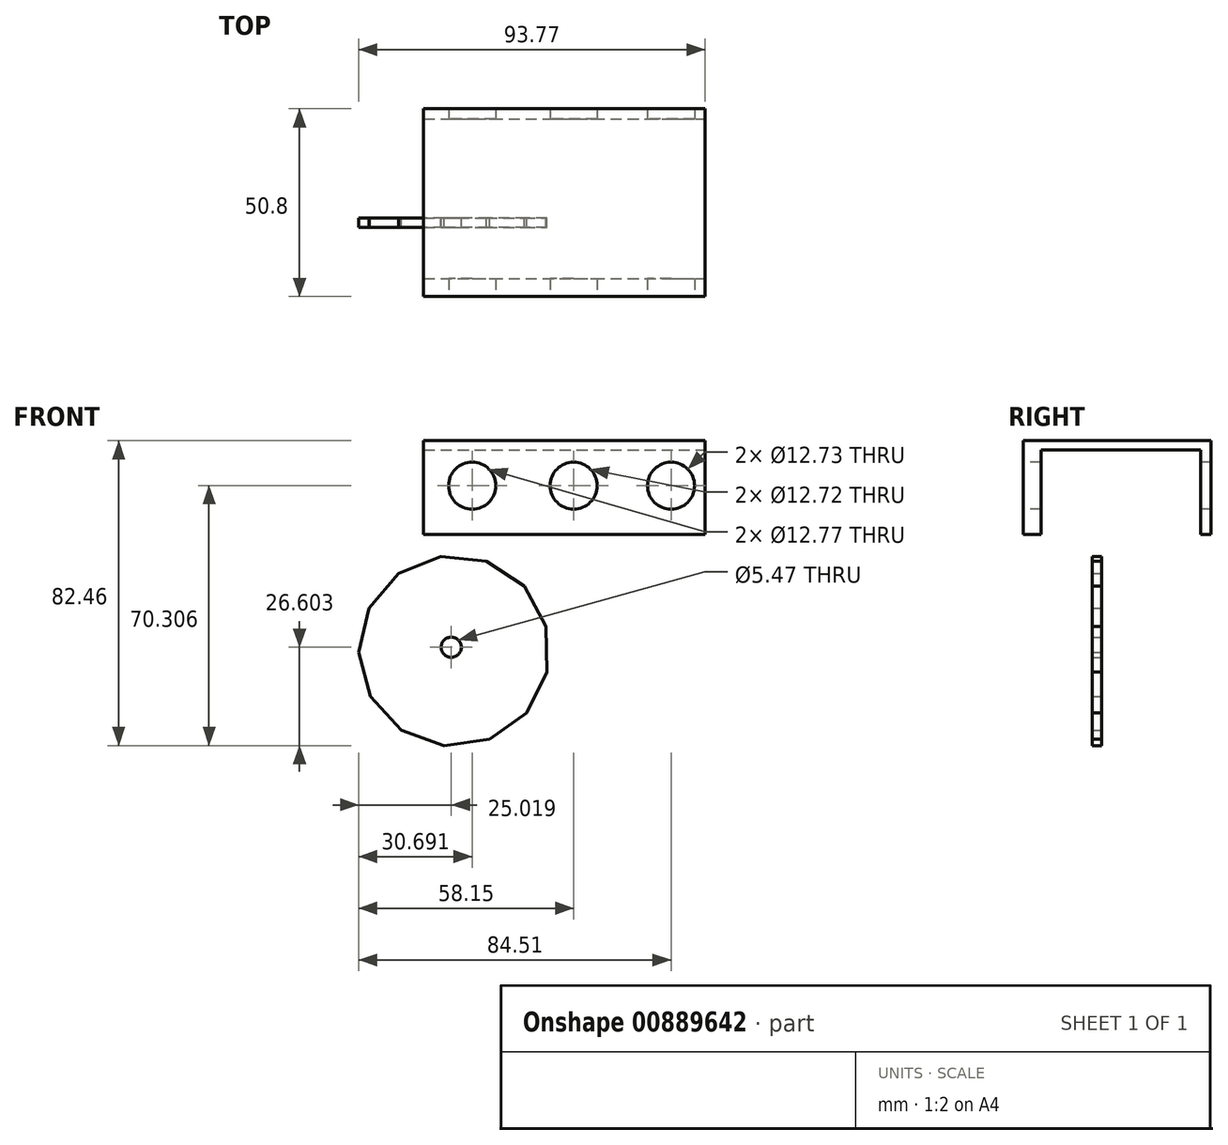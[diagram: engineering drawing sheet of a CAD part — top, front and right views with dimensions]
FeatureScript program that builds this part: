
annotation { "Feature Type Name" : "Feature", "Feature Type Description" : "" }
export const myFeature = defineFeature(function(context is Context, id is Id, definition is map)
    precondition{}
    {
        {
            var Q0;
            Q0=qCreatedBy(makeId("Top.planeOp"),FACE);
            var sketch = newSketch(context, id + "F0", { "sketchPlane" : qUnion([Q0])});
            skLineSegment(sketch, "E0.bottom", {"start": v(-40.58, 29.57) * mm, "end": v(35.62, 29.57) * mm});
            skLineSegment(sketch, "E0.top", {"start": v(-40.58, -21.23) * mm, "end": v(35.62, -21.23) * mm});
            skLineSegment(sketch, "E0.left", {"start": v(-40.58, 29.57) * mm, "end": v(-40.58, -21.23) * mm});
            skLineSegment(sketch, "E0.right", {"start": v(35.62, 29.57) * mm, "end": v(35.62, -21.23) * mm});
            skSolve(sketch);
        }
        {
            var Q0;
            Q0=makeQuery(id+"F0.imprint","IMPRINT",FACE,{"disambiguationData":[TD([[makeQuery(id+"F0.imprint","IMPRINT",EDGE,{"derivedFrom":sQuery(id+"F0.wireOp",EDGE,"E0.bottom")}),-1.0]])]});
            extrude(context, id + "F1", {"entities" : qUnion([Q0]), "depth" : 25.4 * mm, "offsetDistance" : 25.4 * mm});
        }
        {
            var Q0;
            Q0=makeQuery(id+"F1.opExtrude","CAP_FACE",FACE,{"disambiguationData":[OSD([sQuery(id+"F0.wireOp",EDGE,"E0.bottom"),sQuery(id+"F0.wireOp",EDGE,"E0.top"),sQuery(id+"F0.wireOp",EDGE,"E0.left"),sQuery(id+"F0.wireOp",EDGE,"E0.right")])],"isStart":true});
            var sketch = newSketch(context, id + "F2", { "sketchPlane" : qUnion([Q0])});
            skLineSegment(sketch, "E1.bottom", {"start": v(-40.58, 16.4) * mm, "end": v(35.62, 16.4) * mm});
            skLineSegment(sketch, "E1.top", {"start": v(-40.58, -26.78) * mm, "end": v(35.62, -26.78) * mm});
            skLineSegment(sketch, "E1.left", {"start": v(-40.58, 16.4) * mm, "end": v(-40.58, -26.78) * mm});
            skLineSegment(sketch, "E1.right", {"start": v(35.62, 16.4) * mm, "end": v(35.62, -26.78) * mm});
            skSolve(sketch);
        }
        {
            var Q0;
            Q0=makeQuery(id+"F2.imprint","IMPRINT",FACE,{"disambiguationData":[TD([[makeQuery(id+"F2.imprint","IMPRINT",EDGE,{"derivedFrom":sQuery(id+"F2.wireOp",EDGE,"E1.bottom")}),-1.0]])]});
            extrude(context, id + "F3", {"entities" : qUnion([Q0]), "operationType" : NewBodyOperationType.REMOVE, "oppositeDirection" : true, "depth" : 22.86 * mm, "offsetDistance" : 25.4 * mm});
        }
        {
            var Q0;
            Q0=makeQuery(id+"F1.opExtrude","SWEPT_FACE",FACE,{"disambiguationData":[OSD([sQuery(id+"F0.wireOp",EDGE,"E0.top")])]});
            var sketch = newSketch(context, id + "F4", { "sketchPlane" : qUnion([Q0])});
            skCircle(sketch, "E2", {"center": v(0, 13.25) * mm, "radius": 6.36 * mm});
            skCircle(sketch, "E3", {"center": v(26.36, 13.25) * mm, "radius": 6.37 * mm});
            skCircle(sketch, "E4", {"center": v(-27.46, 13.25) * mm, "radius": 6.38 * mm});
            skSolve(sketch);
        }
        {
            var Q0;
            Q0=makeQuery(id+"F4.imprint","IMPRINT",FACE,{"disambiguationData":[TD([[makeQuery(id+"F4.imprint","IMPRINT",EDGE,{"derivedFrom":sQuery(id+"F4.wireOp",EDGE,"E4")}),1.0]])]});
            var Q1;
            Q1=makeQuery(id+"F4.imprint","IMPRINT",FACE,{"disambiguationData":[TD([[makeQuery(id+"F4.imprint","IMPRINT",EDGE,{"derivedFrom":sQuery(id+"F4.wireOp",EDGE,"E2")}),1.0]])]});
            var Q2;
            Q2=makeQuery(id+"F4.imprint","IMPRINT",FACE,{"disambiguationData":[TD([[makeQuery(id+"F4.imprint","IMPRINT",EDGE,{"derivedFrom":sQuery(id+"F4.wireOp",EDGE,"E3")}),1.0]])]});
            extrude(context, id + "F5", {"entities" : qUnion([Q0, Q1, Q2]), "operationType" : NewBodyOperationType.REMOVE, "oppositeDirection" : true, "depth" : 78.74 * mm, "offsetDistance" : 25.4 * mm});
        }
        {
            var Q0;
            Q0=qCreatedBy(makeId("Front.planeOp"),FACE);
            var sketch = newSketch(context, id + "F6", { "sketchPlane" : qUnion([Q0])});
            skCircle(sketch, "E5.cCircle", {"center": v(-32.37, -31.41) * mm, "radius": 25.04 * mm, "construction": true});
            skLineSegment(sketch, "E5.0", {"start": v(-13.37, -13.97) * mm, "end": v(-7.44, -24.8) * mm});
            skLineSegment(sketch, "E5.1", {"start": v(-7.44, -24.8) * mm, "end": v(-7.22, -37.14) * mm});
            skLineSegment(sketch, "E5.2", {"start": v(-7.22, -37.14) * mm, "end": v(-12.76, -48.17) * mm});
            skLineSegment(sketch, "E5.3", {"start": v(-12.76, -48.17) * mm, "end": v(-22.8, -55.36) * mm});
            skLineSegment(sketch, "E5.4", {"start": v(-22.8, -55.36) * mm, "end": v(-35.02, -57.06) * mm});
            skLineSegment(sketch, "E5.5", {"start": v(-35.02, -57.06) * mm, "end": v(-46.64, -52.9) * mm});
            skLineSegment(sketch, "E5.6", {"start": v(-46.64, -52.9) * mm, "end": v(-54.98, -43.8) * mm});
            skLineSegment(sketch, "E5.7", {"start": v(-54.98, -43.8) * mm, "end": v(-58.15, -31.87) * mm});
            skLineSegment(sketch, "E5.8", {"start": v(-58.15, -31.87) * mm, "end": v(-55.41, -19.84) * mm});
            skLineSegment(sketch, "E5.9", {"start": v(-55.41, -19.84) * mm, "end": v(-47.4, -10.45) * mm});
            skLineSegment(sketch, "E5.10", {"start": v(-47.4, -10.45) * mm, "end": v(-35.93, -5.87) * mm});
            skLineSegment(sketch, "E5.11", {"start": v(-35.93, -5.87) * mm, "end": v(-23.65, -7.14) * mm});
            skLineSegment(sketch, "E5.12", {"start": v(-23.65, -7.14) * mm, "end": v(-13.37, -13.97) * mm});
            skPoint(sketch, "E5.0.midPoint", {"position": v(-10.4, -19.38) * mm});
            skSolve(sketch);
        }
        {
            var Q0;
            Q0=makeQuery(id+"F6.imprint","IMPRINT",FACE,{"disambiguationData":[TD([[makeQuery(id+"F6.imprint","IMPRINT",EDGE,{"derivedFrom":sQuery(id+"F6.wireOp",EDGE,"E5.0")}),-1.0]])]});
            extrude(context, id + "F7", {"entities" : qUnion([Q0]), "depth" : 2.54 * mm, "offsetDistance" : 25.4 * mm});
        }
        {
            var Q0;
            Q0=makeQuery(id+"F7.opExtrude","CAP_FACE",FACE,{"disambiguationData":[OSD([sQuery(id+"F6.wireOp",EDGE,"E5.0"),sQuery(id+"F6.wireOp",EDGE,"E5.1"),sQuery(id+"F6.wireOp",EDGE,"E5.2"),sQuery(id+"F6.wireOp",EDGE,"E5.3"),sQuery(id+"F6.wireOp",EDGE,"E5.4"),sQuery(id+"F6.wireOp",EDGE,"E5.5"),sQuery(id+"F6.wireOp",EDGE,"E5.6"),sQuery(id+"F6.wireOp",EDGE,"E5.7"),sQuery(id+"F6.wireOp",EDGE,"E5.8"),sQuery(id+"F6.wireOp",EDGE,"E5.9"),sQuery(id+"F6.wireOp",EDGE,"E5.10"),sQuery(id+"F6.wireOp",EDGE,"E5.11"),sQuery(id+"F6.wireOp",EDGE,"E5.12")])],"isStart":true});
            var sketch = newSketch(context, id + "F8", { "sketchPlane" : qUnion([Q0])});
            skCircle(sketch, "E6", {"center": v(33.13, -30.46) * mm, "radius": 2.73 * mm});
            skSolve(sketch);
        }
        {
            var Q0;
            Q0 = qSketchRegion(id + "F8", true);
            extrude(context, id + "F9", {"entities" : qUnion([Q0]), "operationType" : NewBodyOperationType.REMOVE, "oppositeDirection" : true, "depth" : 25.4 * mm, "offsetDistance" : 25.4 * mm});
        }
    });
